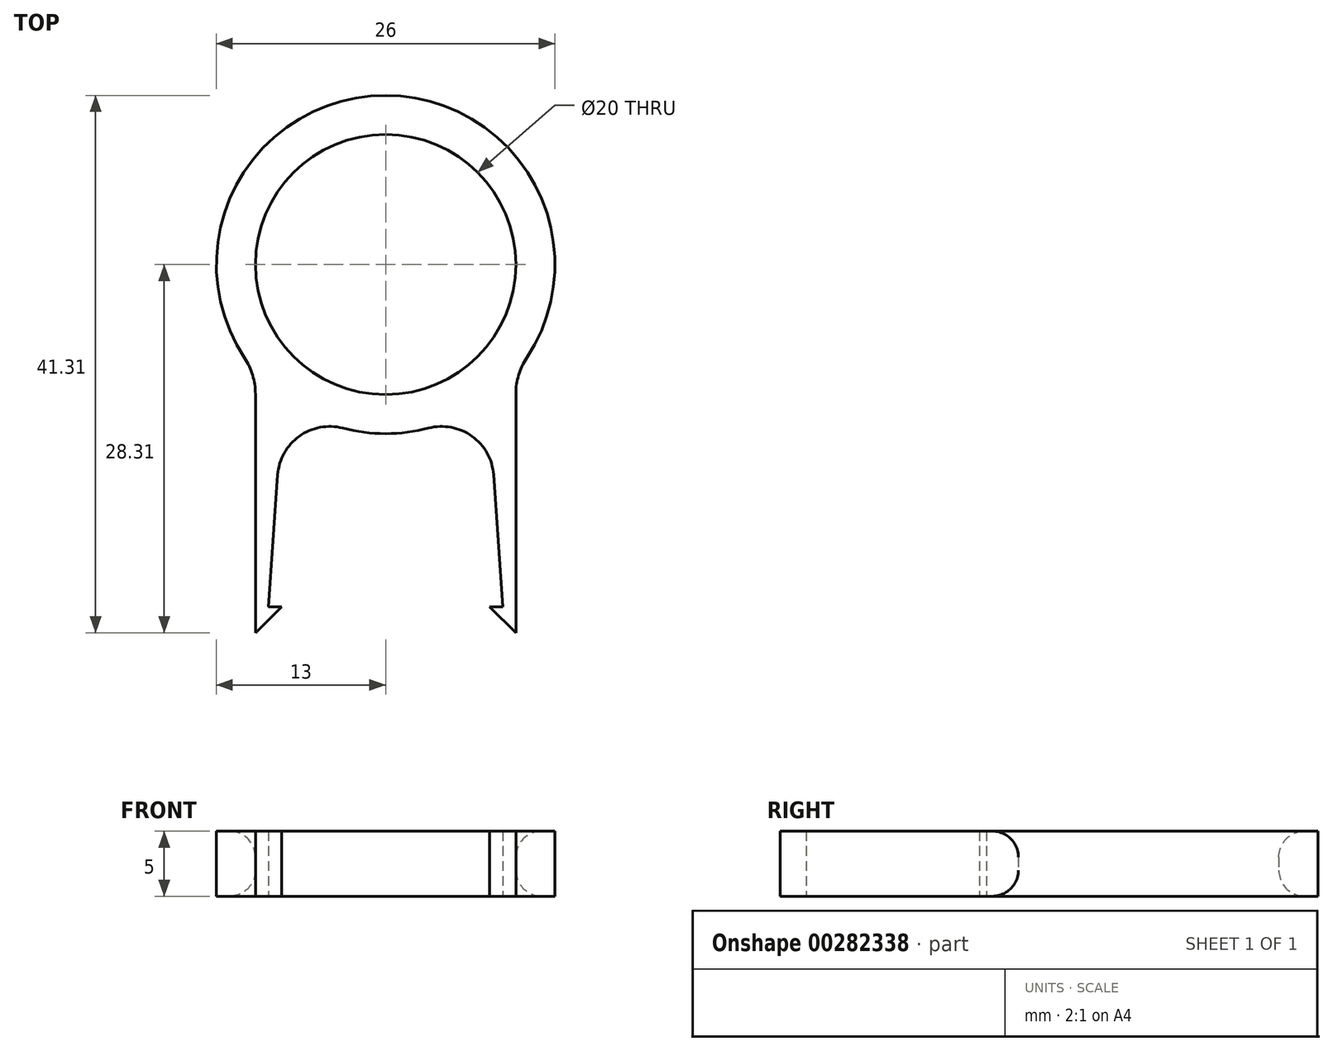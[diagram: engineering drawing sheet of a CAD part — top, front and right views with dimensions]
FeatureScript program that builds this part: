
annotation { "Feature Type Name" : "Feature", "Feature Type Description" : "" }
export const myFeature = defineFeature(function(context is Context, id is Id, definition is map)
    precondition{}
    {
        {
            var Q0;
            Q0=qCreatedBy(makeId("Top.planeOp"),FACE);
            var sketch = newSketch(context, id + "F0", { "sketchPlane" : qUnion([Q0])});
            skCircle(sketch, "E0", {"center": v(0, 0) * mm, "radius": 10 * mm});
            skArc(sketch, "E1", {"start": v(-3.29, -12.58) * mm, "mid": v(-1.66, -12.9) * mm, "end": v(0, -13) * mm});
            skLineSegment(sketch, "E2", {"start": v(0, 0) * mm, "end": v(0, -13) * mm, "construction": true});
            skLineSegment(sketch, "E3", {"start": v(-10, -9.95) * mm, "end": v(-10, -28.3) * mm});
            skLineSegment(sketch, "E4", {"start": v(-8, -26.3) * mm, "end": v(-9, -26.3) * mm});
            skLineSegment(sketch, "E5", {"start": v(-9, -26.3) * mm, "end": v(-8.3, -16.17) * mm});
            skArc(sketch, "E6.trimOffspring", {"start": v(10.47, -7.7) * mm, "mid": v(0.32, 13) * mm, "end": v(-10.83, -7.19) * mm});
            skPoint(sketch, "E7.visualSharp", {"position": v(-10, -8.3) * mm});
            skArc(sketch, "E7.filletArc", {"start": v(-10, -9.95) * mm, "mid": v(-10.21, -8.5) * mm, "end": v(-10.83, -7.19) * mm});
            skPoint(sketch, "E8.visualSharp", {"position": v(-7.88, -10.34) * mm});
            skArc(sketch, "E9.MirrorCS", {"start": v(3.29, -12.58) * mm, "mid": v(1.66, -12.9) * mm, "end": v(0, -13) * mm});
            skLineSegment(sketch, "E10.MirrorCS", {"start": v(9, -26.3) * mm, "end": v(8.3, -16.17) * mm});
            skLineSegment(sketch, "E11.MirrorCS", {"start": v(8, -26.3) * mm, "end": v(9, -26.3) * mm});
            skLineSegment(sketch, "E12.MirrorCS", {"start": v(10, -9.95) * mm, "end": v(10, -28.3) * mm});
            skLineSegment(sketch, "E13.MirrorCS", {"start": v(10, -28.3) * mm, "end": v(8, -26.3) * mm});
            skArc(sketch, "E14.MirrorCS", {"start": v(10, -9.95) * mm, "mid": v(10.21, -8.5) * mm, "end": v(10.83, -7.19) * mm});
            skArc(sketch, "E15.filletArc", {"start": v(-3.29, -12.58) * mm, "mid": v(-6.63, -13.2) * mm, "end": v(-8.3, -16.17) * mm});
            skPoint(sketch, "E16.visualSharp", {"position": v(7.88, -10.34) * mm});
            skArc(sketch, "E16.filletArc", {"start": v(8.3, -16.17) * mm, "mid": v(6.63, -13.2) * mm, "end": v(3.29, -12.58) * mm});
            skLineSegment(sketch, "E17", {"start": v(-10, -28.3) * mm, "end": v(-8, -26.3) * mm});
            skSolve(sketch);
        }
        {
            var Q0;
            Q0=makeQuery(id+"F0.imprint","IMPRINT",FACE,{"disambiguationData":[TD([[makeQuery(id+"F0.imprint","IMPRINT",EDGE,{"derivedFrom":sQuery(id+"F0.wireOp",EDGE,"E0")}),-1.0]])]});
            extrude(context, id + "F1", {"entities" : qUnion([Q0]), "depth" : 5 * mm});
        }
        {
            var Q0;
            Q0=makeQuery(id+"F1.opExtrude","CAP_EDGE",EDGE,{"disambiguationData":[OSD([sQuery(id+"F0.wireOp",EDGE,"E0")])],"isStart":true});
            var Q1;
            Q1=makeQuery(id+"F1.opExtrude","CAP_EDGE",EDGE,{"disambiguationData":[OSD([sQuery(id+"F0.wireOp",EDGE,"E0")])],"isStart":false});
            fillet(context, id + "F2", {"entities" : qUnion([Q0, Q1]), "radius" : 2 * mm, "tangentPropagation" : true, "allowEdgeOverflow" : false});
        }
    });
